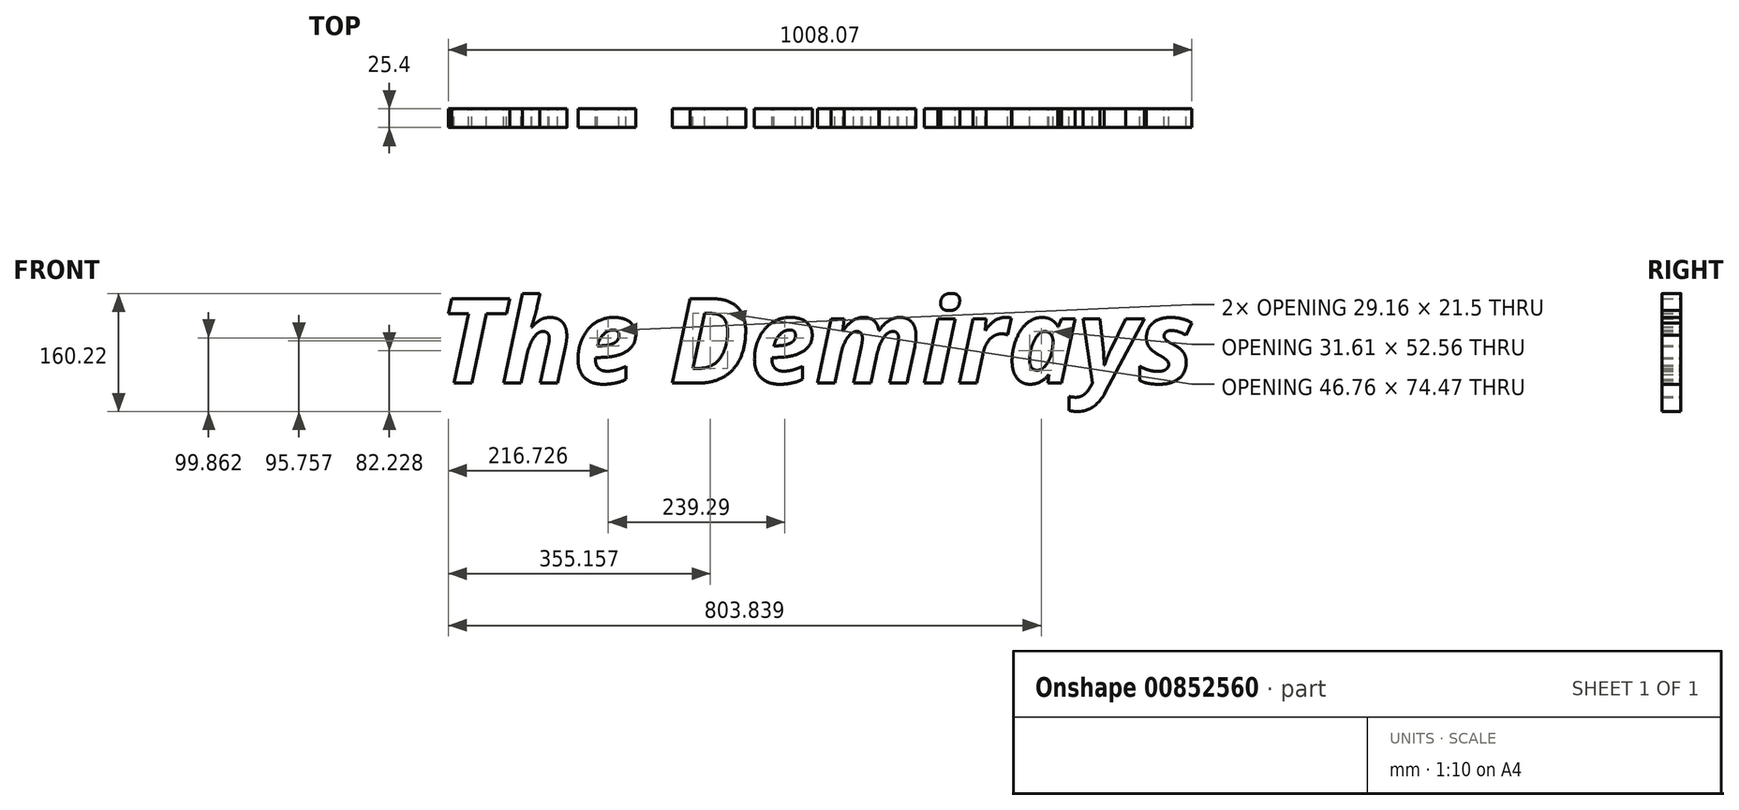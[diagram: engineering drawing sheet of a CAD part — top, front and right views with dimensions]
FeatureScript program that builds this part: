
annotation { "Feature Type Name" : "Feature", "Feature Type Description" : "" }
export const myFeature = defineFeature(function(context is Context, id is Id, definition is map)
    precondition{}
    {
        {
            var Q0;
            Q0=qCreatedBy(makeId("Front.planeOp"),FACE);
            var sketch = newSketch(context, id + "F0", { "sketchPlane" : qUnion([Q0])});
            skText(sketch, "E0", { "text": "The Demirays", "fontName": "OpenSans-BoldItalic.ttf"});
            const initialGuessF0  = {"E0": [-0.13043, -0.07219, 1, 0, 0.11534]};
            skSetInitialGuess(sketch, initialGuessF0);
            skSolve(sketch);
        }
        {
            var Q0;
            Q0 = qSketchRegion(id + "F0", true);
            extrude(context, id + "F1", {"entities" : qUnion([Q0]), "depth" : 25.4 * mm, "offsetDistance" : 25.4 * mm});
        }
    });
